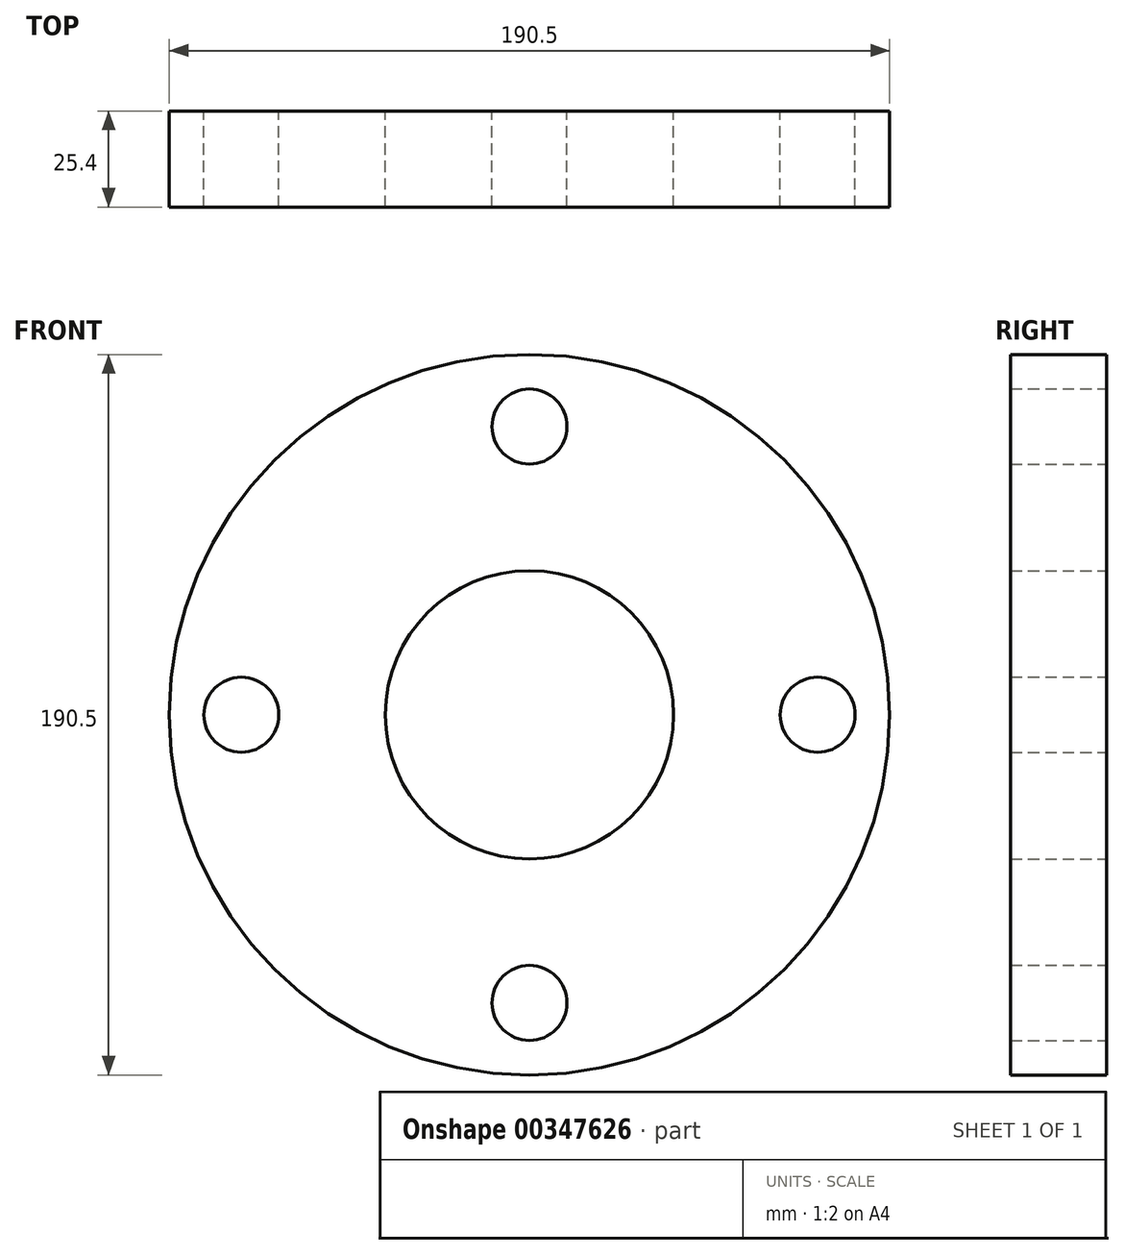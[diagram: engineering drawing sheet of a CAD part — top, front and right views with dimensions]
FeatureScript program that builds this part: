
annotation { "Feature Type Name" : "Feature", "Feature Type Description" : "" }
export const myFeature = defineFeature(function(context is Context, id is Id, definition is map)
    precondition{}
    {
        {
            var Q0;
            Q0=qCreatedBy(makeId("Front.planeOp"),FACE);
            var sketch = newSketch(context, id + "F0", { "sketchPlane" : qUnion([Q0])});
            skCircle(sketch, "E0", {"center": v(0, 0) * mm, "radius": 38.1 * mm});
            skCircle(sketch, "E1", {"center": v(0, 0) * mm, "radius": 95.25 * mm});
            skCircle(sketch, "E2", {"center": v(0, 0) * mm, "radius": 76.2 * mm, "construction": true});
            skLineSegment(sketch, "E3", {"start": v(0, -76.2) * mm, "end": v(0, 76.2) * mm, "construction": true});
            skLineSegment(sketch, "E4", {"start": v(-76.2, 0) * mm, "end": v(76.2, 0) * mm, "construction": true});
            skPoint(sketch, "E5", {"position": v(-76.2, 0) * mm});
            skPoint(sketch, "E6", {"position": v(0, 76.2) * mm});
            skPoint(sketch, "E7", {"position": v(76.2, 0) * mm});
            skPoint(sketch, "E8", {"position": v(0, -76.2) * mm});
            skSolve(sketch);
        }
        {
            var Q0;
            Q0=makeQuery(id+"F0.imprint","IMPRINT",FACE,{"disambiguationData":[TD([[makeQuery(id+"F0.imprint","IMPRINT",EDGE,{"derivedFrom":sQuery(id+"F0.wireOp",EDGE,"E0")}),-1.0]])]});
            extrude(context, id + "F1", {"entities" : qUnion([Q0]), "depth" : 25.4 * mm, "offsetDistance" : 25.4 * mm});
        }
        {
            var Q0;
            Q0=sQuery(id+"F0.wireOp",VERTEX,"E5");
            var Q1;
            Q1=sQuery(id+"F0.wireOp",VERTEX,"E6");
            var Q2;
            Q2=sQuery(id+"F0.wireOp",VERTEX,"E7");
            var Q3;
            Q3=sQuery(id+"F0.wireOp",VERTEX,"E8");
            var Q4;
            Q4=makeQuery(id+"F1.opExtrude","SWEPT_BODY",BODY,{"disambiguationData":[OSD([sQuery(id+"F0.wireOp",EDGE,"E0"),sQuery(id+"F0.wireOp",EDGE,"E1")])]});
            hole(context, id + "F2", {"style" : HoleStyle.SIMPLE, "endStyle" : HoleEndStyle.THROUGH, "oppositeDirection" : true, "standardTappedOrClearance" : lookupTablePath({ "fit" : "Free", "standard" : "ANSI", "size" : "3/4", "type" : "Clearance" }), "standardBlindInLast" : lookupTablePath({ "fit" : "Free", "standard" : "ANSI", "engagement" : "75%", "pitch" : "10 tpi", "size" : "3/4", "type" : "Clearance & tapped" }), "holeDiameter" : 19.84 * mm, "majorDiameter" : 6.35 * mm, "isTappedThrough" : true, "tappedDepth" : 12.7 * mm, "tapClearance" : 3, "startFromSketch" : true, "locations" : qUnion([Q0, Q1, Q2, Q3]), "scope" : qUnion([Q4])});
        }
    });
